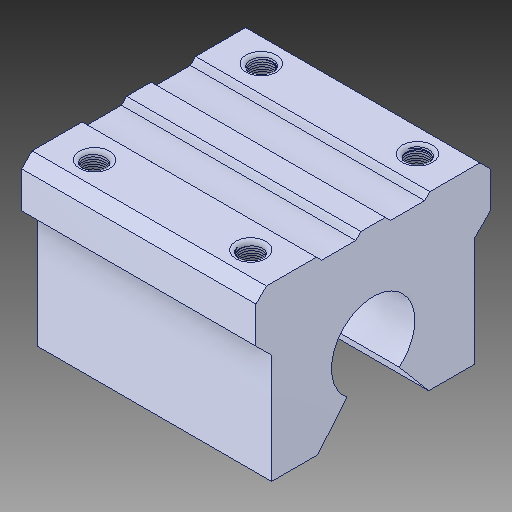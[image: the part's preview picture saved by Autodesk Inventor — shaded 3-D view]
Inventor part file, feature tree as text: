
AUTODESK INVENTOR PART (.ipt)
format: ipt  version: 2018 (Build 220112000, 112)  size: 792,576 bytes
history: native  units: mm
features: other x1, mirror x1
ambient origin geometry x8: Origin, YZ Plane, XZ Plane, XY Plane, X Axis, Y Axis, Z Axis, Center Point
bodies: Body1 (feature_tree)
feature tree (2):
  other  "Sólido1"
  mirror  "Mirror2"
